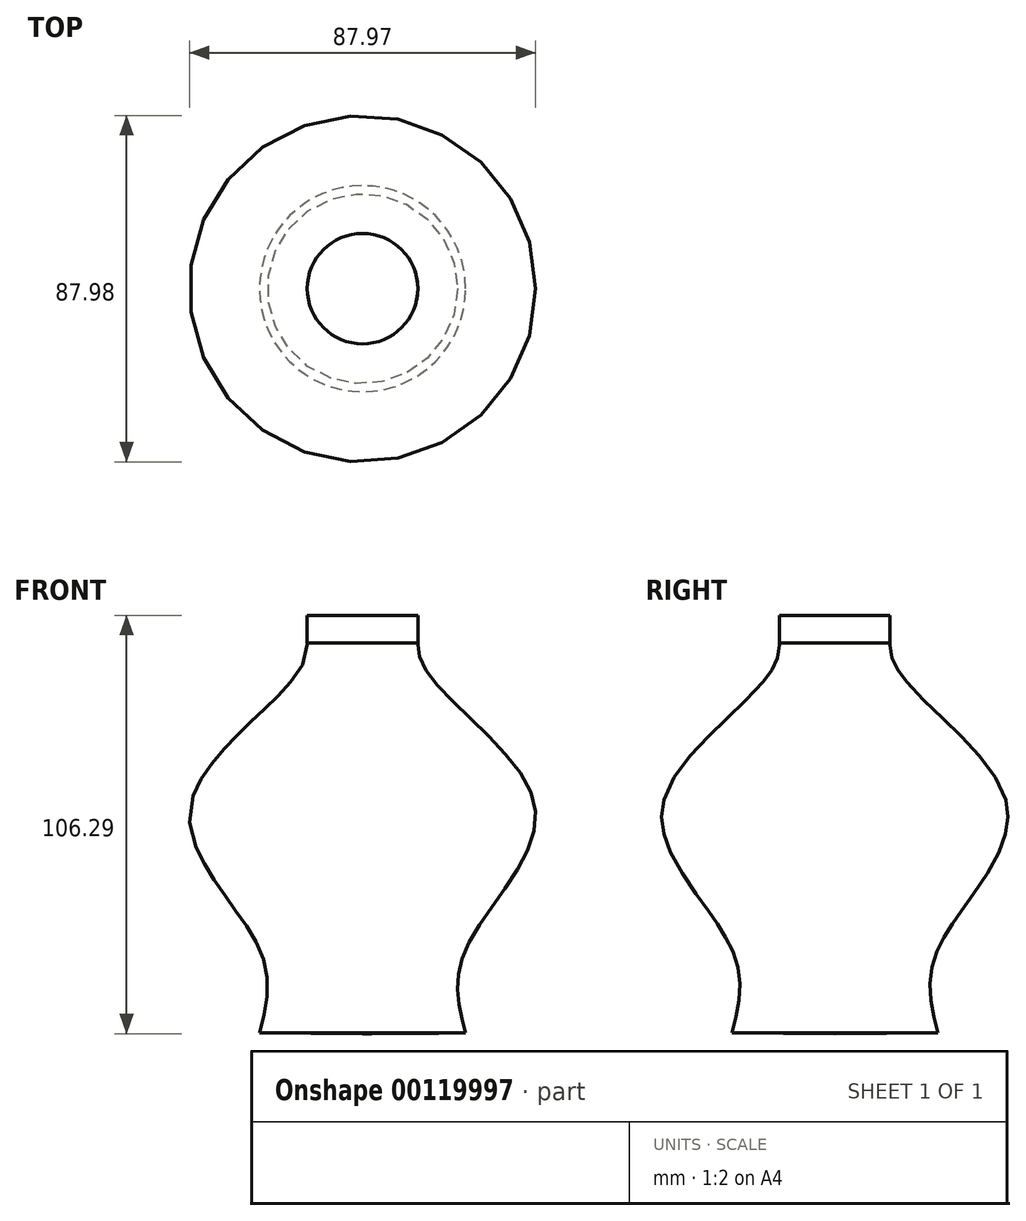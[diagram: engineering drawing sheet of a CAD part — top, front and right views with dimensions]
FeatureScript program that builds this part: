
annotation { "Feature Type Name" : "Feature", "Feature Type Description" : "" }
export const myFeature = defineFeature(function(context is Context, id is Id, definition is map)
    precondition{}
    {
        {
            var Q0;
            Q0=qCreatedBy(makeId("Front.planeOp"),FACE);
            var sketch = newSketch(context, id + "F0", { "sketchPlane" : qUnion([Q0])});
            skLineSegment(sketch, "E0", {"start": v(0, 50.12) * mm, "end": v(0, -56.17) * mm});
            skLineSegment(sketch, "E1", {"start": v(0, -56.17) * mm, "end": v(26.18, -55.98) * mm});
            skFitSpline(sketch, "E2", {"points": [v(26.18, -55.98) * mm, v(26.18, -34.68) * mm, v(43.77, 1.66) * mm, v(15.04, 38) * mm, v(14.07, 45.04) * mm, v(12.5, 42.89) * mm], "startDerivative": vector(-25.37, 96.52) * mm, "endDerivative": vector(-27.9, -44.8) * mm});
            skLineSegment(sketch, "E3", {"start": v(14.04, 42.55) * mm, "end": v(14.04, 50.12) * mm});
            skLineSegment(sketch, "E4", {"start": v(0, 50.12) * mm, "end": v(14.04, 50.12) * mm});
            skSolve(sketch);
        }
        {
            var Q0;
            Q0=makeQuery(id+"F0.imprint","IMPRINT",FACE,{"disambiguationData":[TD([[makeQuery(id+"F0.imprint","IMPRINT",EDGE,{"derivedFrom":sQuery(id+"F0.wireOp",EDGE,"E0")}),1.0]])]});
            var Q1;
            Q1=sQuery(id+"F0.wireOp",EDGE,"E0");
            revolve(context, id + "F1", {"entities" : qUnion([Q0]), "axis" : qUnion([Q1]), "revolveType" : RevolveType.FULL});
        }
    });
